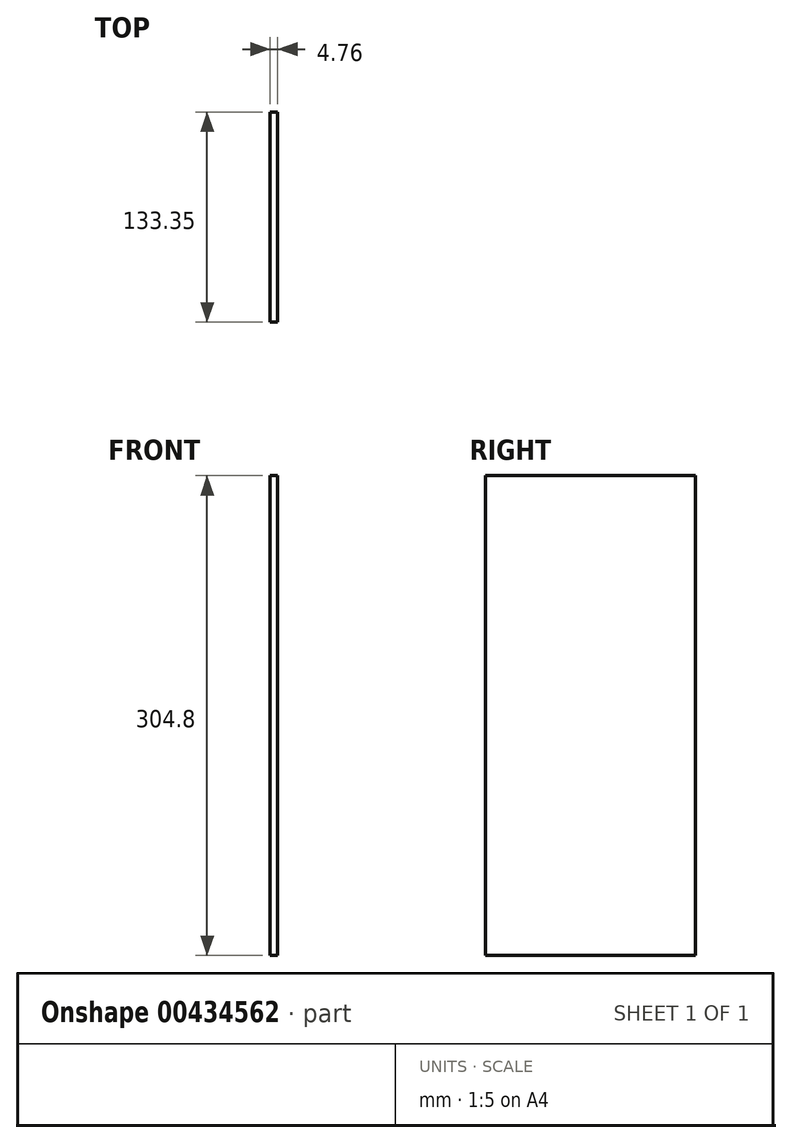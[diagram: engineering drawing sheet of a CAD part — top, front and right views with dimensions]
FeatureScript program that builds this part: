
annotation { "Feature Type Name" : "Feature", "Feature Type Description" : "" }
export const myFeature = defineFeature(function(context is Context, id is Id, definition is map)
    precondition{}
    {
        {
            var Q0;
            Q0=qCreatedBy(makeId("Right.planeOp"),FACE);
            var sketch = newSketch(context, id + "F0", { "sketchPlane" : qUnion([Q0])});
            skLineSegment(sketch, "E0.bottom", {"start": v(-40.74, 313.46) * mm, "end": v(92.6, 313.46) * mm});
            skLineSegment(sketch, "E0.top", {"start": v(-40.74, 8.66) * mm, "end": v(92.6, 8.66) * mm});
            skLineSegment(sketch, "E0.left", {"start": v(-40.74, 313.46) * mm, "end": v(-40.74, 8.66) * mm});
            skLineSegment(sketch, "E0.right", {"start": v(92.6, 313.46) * mm, "end": v(92.6, 8.66) * mm});
            skSolve(sketch);
        }
        {
            var Q0;
            Q0=makeQuery(id+"F0.imprint","IMPRINT",FACE,{"disambiguationData":[TD([[makeQuery(id+"F0.imprint","IMPRINT",EDGE,{"derivedFrom":sQuery(id+"F0.wireOp",EDGE,"E0.bottom")}),-1.0]])]});
            extrude(context, id + "F1", {"entities" : qUnion([Q0]), "depth" : 4.76 * mm});
        }
    });
